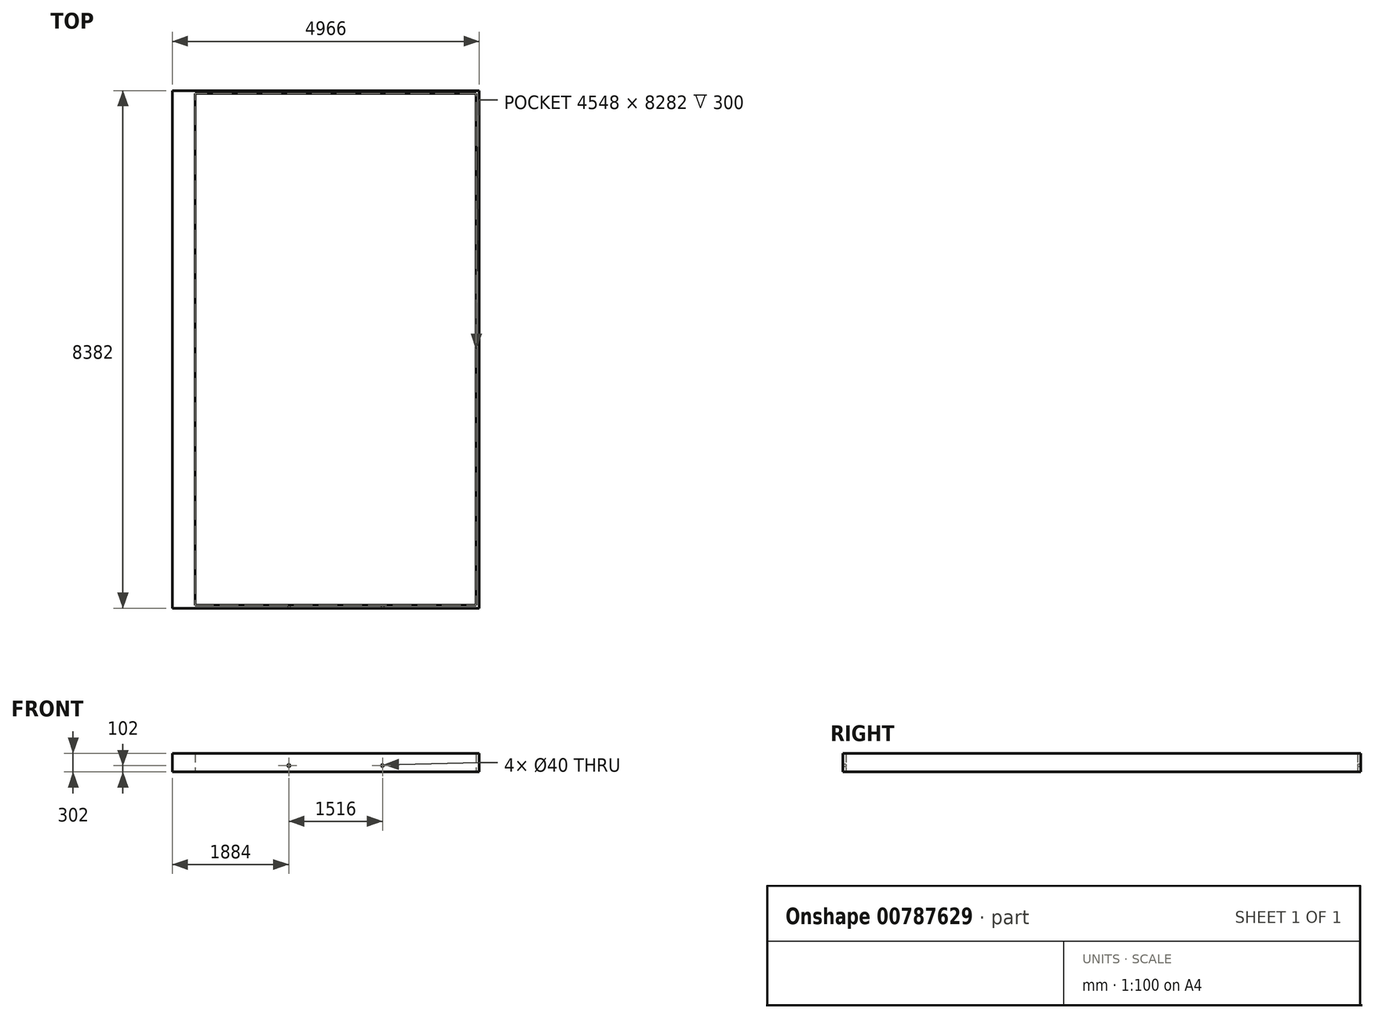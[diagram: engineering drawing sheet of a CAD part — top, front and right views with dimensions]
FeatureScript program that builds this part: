
annotation { "Feature Type Name" : "Feature", "Feature Type Description" : "" }
export const myFeature = defineFeature(function(context is Context, id is Id, definition is map)
    precondition{}
    {
        {
            var Q0;
            Q0=qCreatedBy(makeId("Top.planeOp"),FACE);
            var sketch = newSketch(context, id + "F0", { "sketchPlane" : qUnion([Q0])});
            skLineSegment(sketch, "E0.bottom", {"start": v(0, 0) * mm, "end": v(4966, 0) * mm});
            skLineSegment(sketch, "E0.top", {"start": v(0, 8382) * mm, "end": v(4966, 8382) * mm});
            skLineSegment(sketch, "E0.left", {"start": v(0, 0) * mm, "end": v(0, 8382) * mm});
            skLineSegment(sketch, "E0.right", {"start": v(4966, 0) * mm, "end": v(4966, 8382) * mm});
            skLineSegment(sketch, "E1.0", {"start": v(368, 8332) * mm, "end": v(4916, 8332) * mm});
            skLineSegment(sketch, "E2.0", {"start": v(368, 50) * mm, "end": v(4916, 50) * mm});
            skLineSegment(sketch, "E3.0", {"start": v(4916, 50) * mm, "end": v(4916, 8332) * mm});
            skLineSegment(sketch, "E4.0", {"start": v(368, 50) * mm, "end": v(368, 8332) * mm});
            skSolve(sketch);
        }
        {
            var Q0;
            Q0=makeQuery(id+"F0.imprint","IMPRINT",FACE,{"disambiguationData":[TD([[makeQuery(id+"F0.imprint","IMPRINT",EDGE,{"derivedFrom":sQuery(id+"F0.wireOp",EDGE,"E0.bottom")}),1.0]])]});
            extrude(context, id + "F1", {"entities" : qUnion([Q0]), "depth" : 300 * mm, "offsetDistance" : 25 * mm});
        }
        {
            var Q0;
            Q0=makeQuery(id+"F1.opExtrude","CAP_FACE",FACE,{"disambiguationData":[OSD([sQuery(id+"F0.wireOp",EDGE,"E0.bottom"),sQuery(id+"F0.wireOp",EDGE,"E0.top"),sQuery(id+"F0.wireOp",EDGE,"E0.left"),sQuery(id+"F0.wireOp",EDGE,"E0.right"),sQuery(id+"F0.wireOp",EDGE,"E1.0"),sQuery(id+"F0.wireOp",EDGE,"E2.0"),sQuery(id+"F0.wireOp",EDGE,"E3.0"),sQuery(id+"F0.wireOp",EDGE,"E4.0")])],"isStart":true});
            var sketch = newSketch(context, id + "F2", { "sketchPlane" : qUnion([Q0])});
            skLineSegment(sketch, "E5.bottom", {"start": v(0, 0) * mm, "end": v(4966, 0) * mm});
            skLineSegment(sketch, "E5.top", {"start": v(0, -8382) * mm, "end": v(4966, -8382) * mm});
            skLineSegment(sketch, "E5.left", {"start": v(0, 0) * mm, "end": v(0, -8382) * mm});
            skLineSegment(sketch, "E5.right", {"start": v(4966, 0) * mm, "end": v(4966, -8382) * mm});
            skSolve(sketch);
        }
        {
            var Q0;
            Q0 = qSketchRegion(id + "F2", true);
            extrude(context, id + "F3", {"entities" : qUnion([Q0]), "operationType" : NewBodyOperationType.ADD, "depth" : 2 * mm, "offsetDistance" : 25 * mm});
        }
        {
            var Q0;
            Q0=makeQuery(id+"F3.boolean.opBoolean","MERGE",FACE,{"derivedFrom":[makeQuery(id+"F1.opExtrude","SWEPT_FACE",FACE,{"disambiguationData":[OSD([sQuery(id+"F0.wireOp",EDGE,"E0.bottom")])]}),makeQuery(id+"F3.opExtrude","SWEPT_FACE",FACE,{"disambiguationData":[OSD([sQuery(id+"F2.wireOp",EDGE,"E5.bottom")])]})]});
            var sketch = newSketch(context, id + "F4", { "sketchPlane" : qUnion([Q0])});
            skCircle(sketch, "E6", {"center": v(1884, 100) * mm, "radius": 20 * mm});
            skCircle(sketch, "E7", {"center": v(3400, 100) * mm, "radius": 20 * mm});
            skSolve(sketch);
        }
        {
            var Q0;
            Q0 = qSketchRegion(id + "F4", true);
            extrude(context, id + "F5", {"entities" : qUnion([Q0]), "operationType" : NewBodyOperationType.REMOVE, "endBound" : BoundingType.THROUGH_ALL, "oppositeDirection" : true, "depth" : 25 * mm, "offsetDistance" : 25 * mm});
        }
    });
